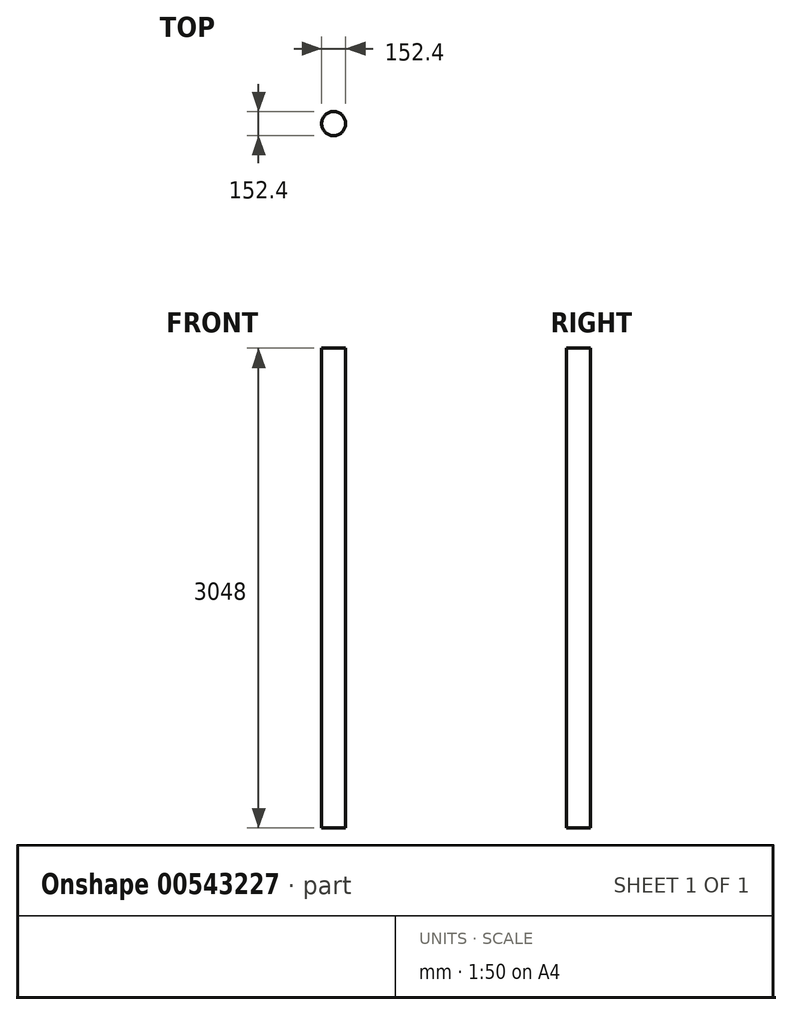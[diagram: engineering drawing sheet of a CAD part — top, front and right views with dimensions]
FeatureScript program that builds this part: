
annotation { "Feature Type Name" : "Feature", "Feature Type Description" : "" }
export const myFeature = defineFeature(function(context is Context, id is Id, definition is map)
    precondition{}
    {
        {
            var Q0;
            Q0=qCreatedBy(makeId("Top.planeOp"),FACE);
            var sketch = newSketch(context, id + "F0", { "sketchPlane" : qUnion([Q0])});
            skCircle(sketch, "E0", {"center": v(0, 0) * mm, "radius": 76.2 * mm});
            skSolve(sketch);
        }
        {
            var Q0;
            Q0=makeQuery(id+"F0.imprint","IMPRINT",FACE,{"disambiguationData":[TD([[makeQuery(id+"F0.imprint","IMPRINT",EDGE,{"derivedFrom":sQuery(id+"F0.wireOp",EDGE,"E0")}),1.0]])]});
            extrude(context, id + "F1", {"entities" : qUnion([Q0]), "depth" : 3048 * mm, "offsetDistance" : 30.48 * mm});
        }
    });
